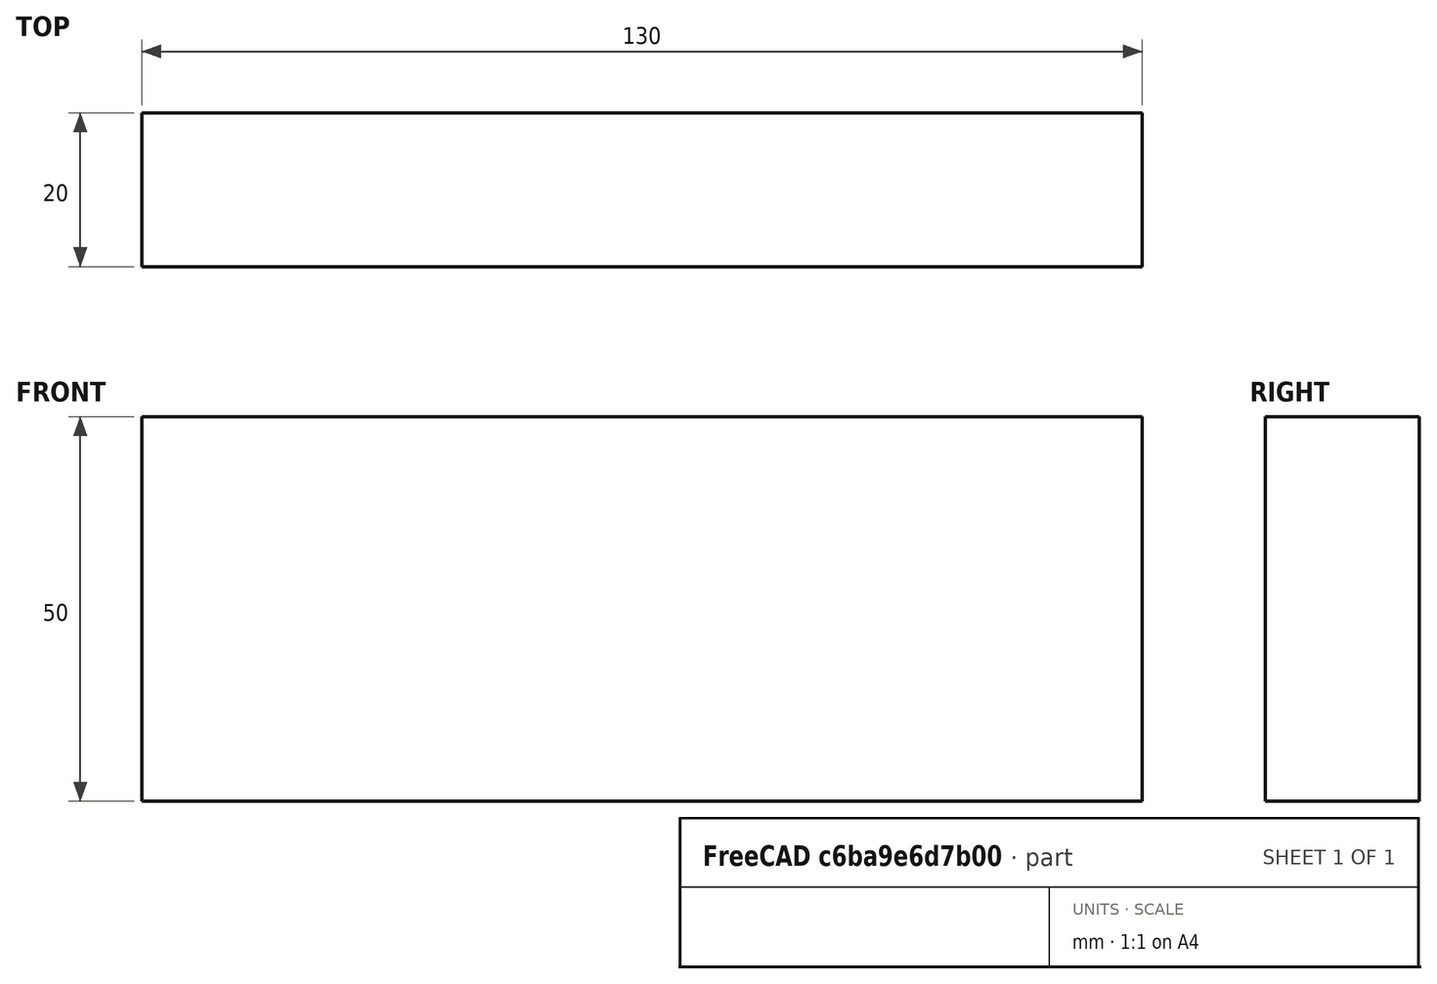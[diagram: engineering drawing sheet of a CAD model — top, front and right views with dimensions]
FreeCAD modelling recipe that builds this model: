
FCSTD DOCUMENT  (FreeCAD 0.15R4671 (Git))
Label: Flat Bar 130x20 EN10058 S235JR
License: All rights reserved
LicenseURL: http://en.wikipedia.org/wiki/All_rights_reserved
objects: Sketcher::SketchObject×1, Part::Extrusion×1
note: 2 computed .brp shape members not serialized (recipe doc carries the construction recipe); baked Part::Feature solids carry a one-line shape summary decoded from their .brp

FEATURE [Sketcher::SketchObject] Sketch
  sketch-geometry (4):
    g0: LineSegment StartX=-65 StartY=-10 StartZ=0 EndX=65 EndY=-10 EndZ=0
    g1: LineSegment StartX=65 StartY=-10 StartZ=0 EndX=65 EndY=10 EndZ=0
    g2: LineSegment StartX=65 StartY=10 StartZ=0 EndX=-65 EndY=10 EndZ=0
    g3: LineSegment StartX=-65 StartY=10 StartZ=0 EndX=-65 EndY=-10 EndZ=0
  constraints (12):
    c: Coincident(g0,g1)
    c: Coincident(g1,g2)
    c: Coincident(g2,g3)
    c: Coincident(g3,g0)
    c: Horizontal(g0)
    c: Horizontal(g2)
    c: Vertical(g1)
    c: Vertical(g3)
    c: Symmetric(g1,g2,g-2)
    c: Symmetric(g0,g1,g-1)
    c: DistanceY(g1) = 20
    c: DistanceX(g0) = 130
FEATURE [Part::Extrusion] Extrude  label="Flat Bar 130x20 EN10058 S235JR"
  Base = -> Sketch
  Dir = (0,0,50)
  Solid = true
